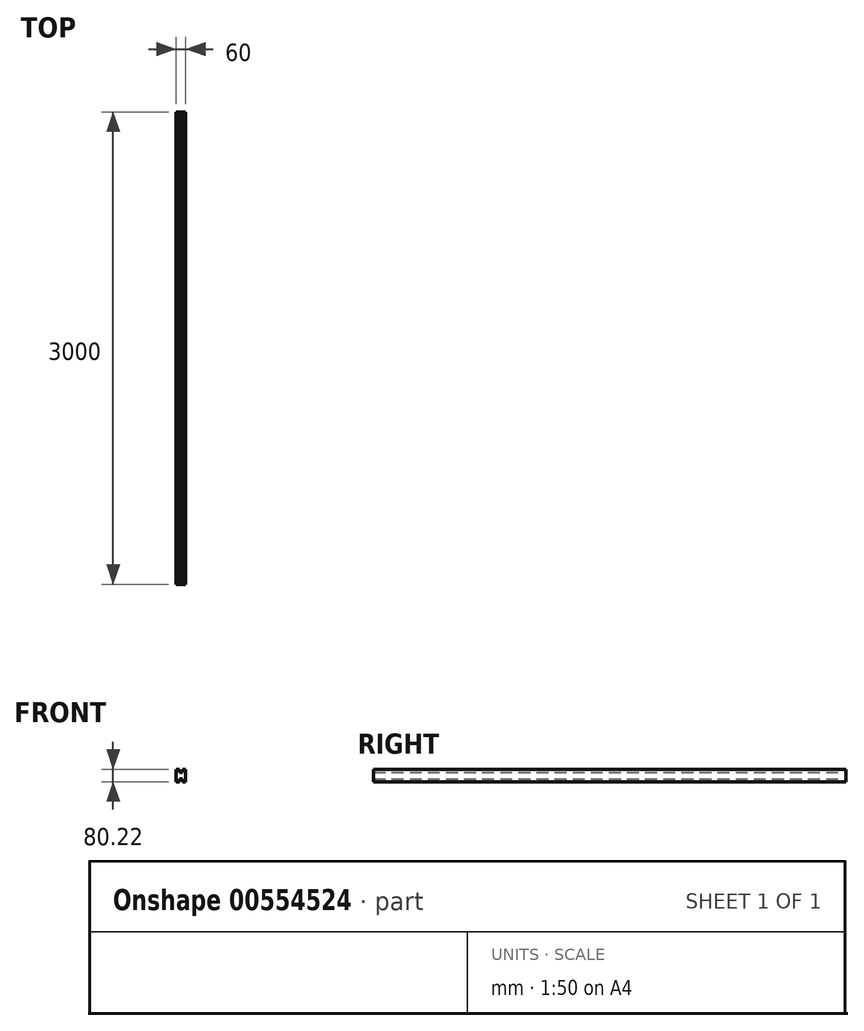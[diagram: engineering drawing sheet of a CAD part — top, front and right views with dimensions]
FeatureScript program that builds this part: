
annotation { "Feature Type Name" : "Feature", "Feature Type Description" : "" }
export const myFeature = defineFeature(function(context is Context, id is Id, definition is map)
    precondition{}
    {
        {
            var Q0;
            Q0=qCreatedBy(makeId("Front.planeOp"),FACE);
            var sketch = newSketch(context, id + "F0", { "sketchPlane" : qUnion([Q0])});
            skLineSegment(sketch, "E0", {"start": v(0, 65.68) * mm, "end": v(0, -14.32) * mm});
            skLineSegment(sketch, "E1", {"start": v(0, -14.32) * mm, "end": v(20, -14.32) * mm});
            skLineSegment(sketch, "E2", {"start": v(20, -14.32) * mm, "end": v(20, 5.68) * mm});
            skLineSegment(sketch, "E3", {"start": v(20, 5.68) * mm, "end": v(40, 5.68) * mm});
            skLineSegment(sketch, "E4", {"start": v(40, 5.68) * mm, "end": v(40, -14.32) * mm});
            skLineSegment(sketch, "E5", {"start": v(40, -14.32) * mm, "end": v(60, -14.32) * mm});
            skLineSegment(sketch, "E6", {"start": v(60, -14.32) * mm, "end": v(60, 65.9) * mm});
            skLineSegment(sketch, "E7", {"start": v(60, 65.9) * mm, "end": v(40, 65.9) * mm});
            skLineSegment(sketch, "E8", {"start": v(40, 65.9) * mm, "end": v(40, 46.27) * mm});
            skLineSegment(sketch, "E9", {"start": v(40, 46.27) * mm, "end": v(19.69, 46.27) * mm});
            skLineSegment(sketch, "E10", {"start": v(19.69, 46.27) * mm, "end": v(19.69, 65.9) * mm});
            skLineSegment(sketch, "E11", {"start": v(19.69, 65.9) * mm, "end": v(0, 65.68) * mm});
            skSolve(sketch);
        }
        {
            var Q0;
            Q0=makeQuery(id+"F0.imprint","IMPRINT",FACE,{"disambiguationData":[TD([[makeQuery(id+"F0.imprint","IMPRINT",EDGE,{"derivedFrom":sQuery(id+"F0.wireOp",EDGE,"E0")}),1.0]])]});
            extrude(context, id + "F1", {"entities" : qUnion([Q0]), "depth" : 3000 * mm, "offsetDistance" : 25 * mm});
        }
    });
